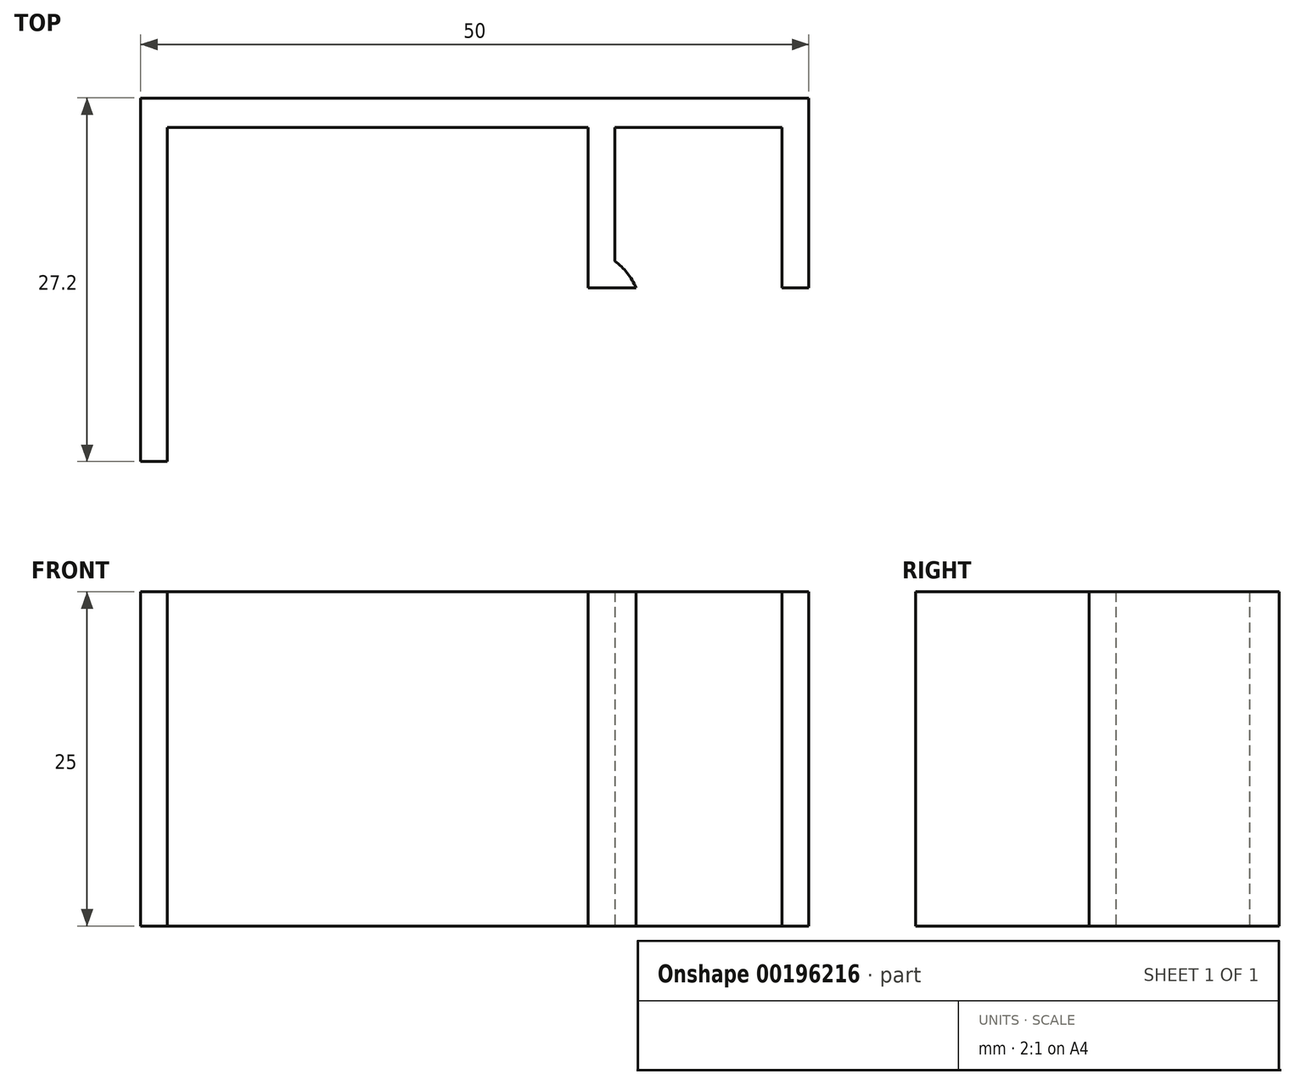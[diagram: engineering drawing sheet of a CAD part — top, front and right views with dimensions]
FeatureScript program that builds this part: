
annotation { "Feature Type Name" : "Feature", "Feature Type Description" : "" }
export const myFeature = defineFeature(function(context is Context, id is Id, definition is map)
    precondition{}
    {
        {
            var Q0;
            Q0=qCreatedBy(makeId("Top.planeOp"),FACE);
            var sketch = newSketch(context, id + "F0", { "sketchPlane" : qUnion([Q0])});
            skLineSegment(sketch, "E0.bottom", {"start": v(-30.81, -17.1) * mm, "end": v(19.19, -17.1) * mm});
            skLineSegment(sketch, "E0.top", {"start": v(-30.81, -19.3) * mm, "end": v(19.19, -19.3) * mm});
            skLineSegment(sketch, "E0.left", {"start": v(-30.81, -17.1) * mm, "end": v(-30.81, -19.3) * mm});
            skLineSegment(sketch, "E0.right", {"start": v(19.19, -17.1) * mm, "end": v(19.19, -19.3) * mm});
            skSolve(sketch);
        }
        {
            var Q0;
            Q0=qSketchRegion(id+"F0",true);
            extrude(context, id + "F1", {"entities" : qUnion([Q0]), "depth" : 25 * mm});
        }
        {
            var Q0;
            Q0=makeQuery(id+"F1.opExtrude","SWEPT_FACE",FACE,{"disambiguationData":[OSD([sQuery(id+"F0.wireOp",EDGE,"E0.top")])]});
            var sketch = newSketch(context, id + "F2", { "sketchPlane" : qUnion([Q0])});
            skLineSegment(sketch, "E1.bottom", {"start": v(19.19, 25) * mm, "end": v(2.69, 25) * mm});
            skLineSegment(sketch, "E1.top", {"start": v(19.19, 0) * mm, "end": v(2.69, 0) * mm});
            skLineSegment(sketch, "E1.left", {"start": v(19.19, 25) * mm, "end": v(19.19, 0) * mm});
            skLineSegment(sketch, "E1.right", {"start": v(2.69, 25) * mm, "end": v(2.69, 0) * mm});
            skLineSegment(sketch, "E2", {"start": v(4.69, 25) * mm, "end": v(4.69, 0) * mm});
            skLineSegment(sketch, "E3", {"start": v(17.19, 25) * mm, "end": v(17.19, 0) * mm});
            skLineSegment(sketch, "E4", {"start": v(-28.81, 25) * mm, "end": v(-28.81, 0) * mm});
            skSolve(sketch);
        }
        {
            var Q0;
            {var subQ0=sQuery(id+"F2.wireOp",EDGE,"E1.right");Q0=makeQuery(id+"F2.imprint","IMPRINT",FACE,{"disambiguationData":[TD([[makeQuery(id+"F2.imprint","IMPRINT",EDGE,{"derivedFrom":subQ0}),1.0]])]});}
            var Q1;
            {var subQ0=sQuery(id+"F2.wireOp",EDGE,"E1.left");Q1=makeQuery(id+"F2.imprint","IMPRINT",FACE,{"disambiguationData":[TD([[makeQuery(id+"F2.imprint","IMPRINT",EDGE,{"derivedFrom":subQ0}),-1.0]])]});}
            extrude(context, id + "F3", {"entities" : qUnion([Q0, Q1]), "operationType" : NewBodyOperationType.ADD, "depth" : 12 * mm});
        }
        {
            var Q0;
            {var subQ0=sQuery(id+"F2.wireOp",EDGE,"E4");Q0=makeQuery(id+"F2.imprint","IMPRINT",FACE,{"disambiguationData":[TD([[makeQuery(id+"F2.imprint","IMPRINT",EDGE,{"derivedFrom":subQ0}),-1.0]])]});}
            extrude(context, id + "F4", {"entities" : qUnion([Q0]), "operationType" : NewBodyOperationType.ADD, "depth" : 25 * mm});
        }
        {
            var Q0;
            Q0=makeQuery(id+"F3.opExtrude","SWEPT_FACE",FACE,{"disambiguationData":[OSD([sQuery(id+"F2.wireOp",EDGE,"E2")])]});
            var sketch = newSketch(context, id + "F5", { "sketchPlane" : qUnion([Q0])});
            skLineSegment(sketch, "E5.bottom", {"start": v(-31.3, 25) * mm, "end": v(-29.3, 25) * mm});
            skLineSegment(sketch, "E5.top", {"start": v(-31.3, 0) * mm, "end": v(-29.3, 0) * mm});
            skLineSegment(sketch, "E5.left", {"start": v(-31.3, 25) * mm, "end": v(-31.3, 0) * mm});
            skLineSegment(sketch, "E5.right", {"start": v(-29.3, 25) * mm, "end": v(-29.3, 0) * mm});
            skSolve(sketch);
        }
        {
            var Q0;
            Q0=makeQuery(id+"F5.imprint","IMPRINT",FACE,{"disambiguationData":[TD([[makeQuery(id+"F5.imprint","IMPRINT",EDGE,{"derivedFrom":sQuery(id+"F5.wireOp",EDGE,"E5.bottom")}),-1.0]])]});
            extrude(context, id + "F6", {"entities" : qUnion([Q0]), "operationType" : NewBodyOperationType.ADD, "depth" : 2 * mm});
        }
        {
            var Q0;
            Q0=makeQuery(id+"F6.opExtrude","CAP_EDGE",EDGE,{"disambiguationData":[OSD([sQuery(id+"F5.wireOp",EDGE,"E5.right")])],"isStart":false});
            fillet(context, id + "F7", {"entities" : qUnion([Q0]), "radius" : 5 * mm, "tangentPropagation" : true, "allowEdgeOverflow" : false});
        }
    });
